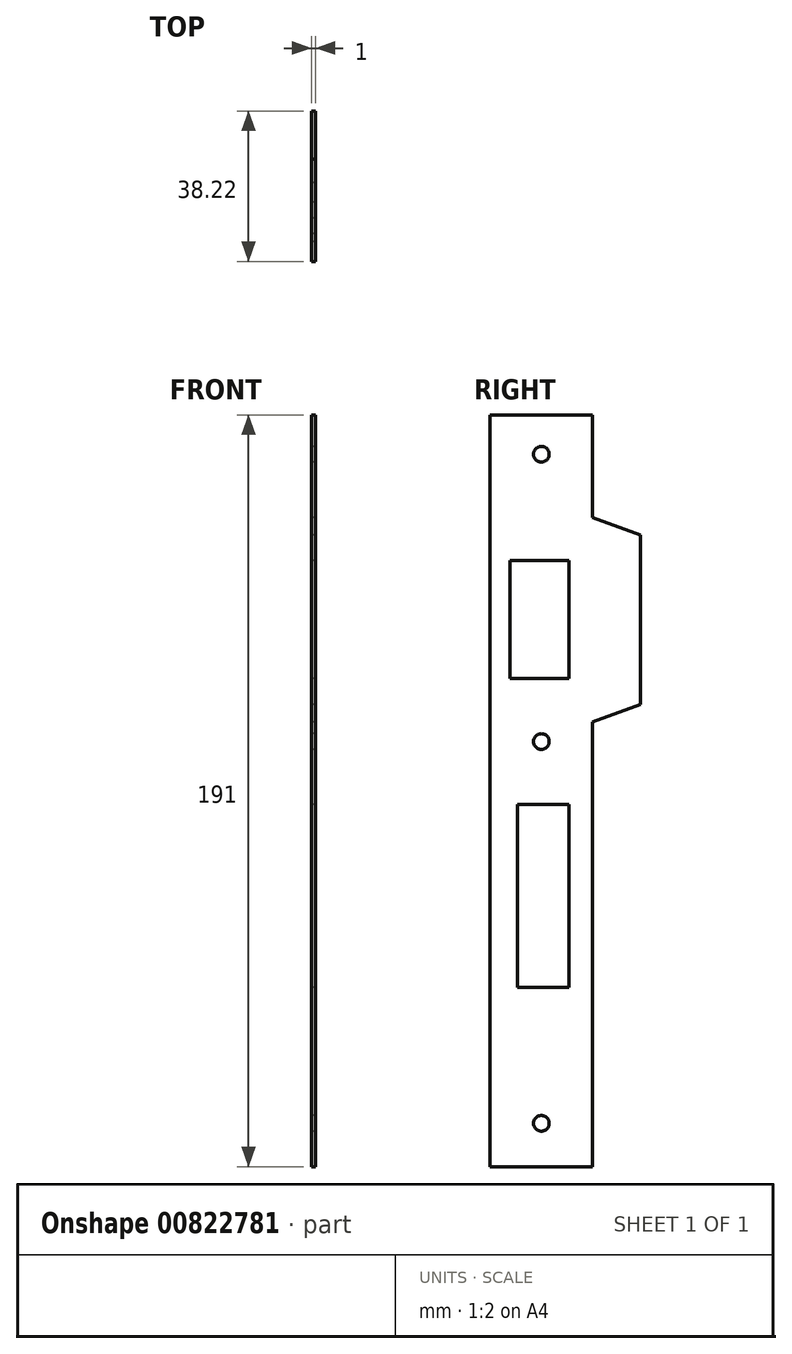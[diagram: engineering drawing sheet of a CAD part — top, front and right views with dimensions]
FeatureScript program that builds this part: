
annotation { "Feature Type Name" : "Feature", "Feature Type Description" : "" }
export const myFeature = defineFeature(function(context is Context, id is Id, definition is map)
    precondition{}
    {
        {
            var Q0;
            Q0=qCreatedBy(makeId("Right.planeOp"),FACE);
            var sketch = newSketch(context, id + "F0", { "sketchPlane" : qUnion([Q0])});
            skLineSegment(sketch, "E0", {"start": v(-5, 97.68) * mm, "end": v(-5, -93.32) * mm});
            skLineSegment(sketch, "E1", {"start": v(-5, -93.32) * mm, "end": v(21, -93.32) * mm});
            skLineSegment(sketch, "E2", {"start": v(21, -93.32) * mm, "end": v(21, 19.68) * mm});
            skLineSegment(sketch, "E3", {"start": v(21, 19.68) * mm, "end": v(33.22, 24.12) * mm});
            skLineSegment(sketch, "E4", {"start": v(33.22, 24.12) * mm, "end": v(33.22, 67.12) * mm});
            skLineSegment(sketch, "E5", {"start": v(33.22, 67.12) * mm, "end": v(21, 71.57) * mm});
            skLineSegment(sketch, "E6", {"start": v(21, 71.57) * mm, "end": v(21, 97.68) * mm});
            skLineSegment(sketch, "E7", {"start": v(21, 97.68) * mm, "end": v(-5, 97.68) * mm});
            skCircle(sketch, "E8", {"center": v(8, 87.68) * mm, "radius": 2 * mm});
            skLineSegment(sketch, "E9.bottom", {"start": v(0, 60.68) * mm, "end": v(15, 60.68) * mm});
            skLineSegment(sketch, "E9.top", {"start": v(0, 30.68) * mm, "end": v(15, 30.68) * mm});
            skLineSegment(sketch, "E9.left", {"start": v(0, 60.68) * mm, "end": v(0, 30.68) * mm});
            skLineSegment(sketch, "E9.right", {"start": v(15, 60.68) * mm, "end": v(15, 30.68) * mm});
            skCircle(sketch, "E10", {"center": v(8, 14.68) * mm, "radius": 2 * mm});
            skLineSegment(sketch, "E11.bottom", {"start": v(2, -1.32) * mm, "end": v(15, -1.32) * mm});
            skLineSegment(sketch, "E11.top", {"start": v(2, -47.82) * mm, "end": v(15, -47.82) * mm});
            skLineSegment(sketch, "E11.left", {"start": v(2, -1.32) * mm, "end": v(2, -47.82) * mm});
            skLineSegment(sketch, "E11.right", {"start": v(15, -1.32) * mm, "end": v(15, -47.82) * mm});
            skCircle(sketch, "E12", {"center": v(8, -82.32) * mm, "radius": 2 * mm});
            skSolve(sketch);
        }
        {
            var Q0;
            Q0=makeQuery(id+"F0.imprint","IMPRINT",FACE,{"disambiguationData":[TD([[makeQuery(id+"F0.imprint","IMPRINT",EDGE,{"derivedFrom":sQuery(id+"F0.wireOp",EDGE,"E0")}),1.0]])]});
            extrude(context, id + "F1", {"entities" : qUnion([Q0]), "depth" : 1 * mm, "offsetDistance" : 25 * mm});
        }
    });
